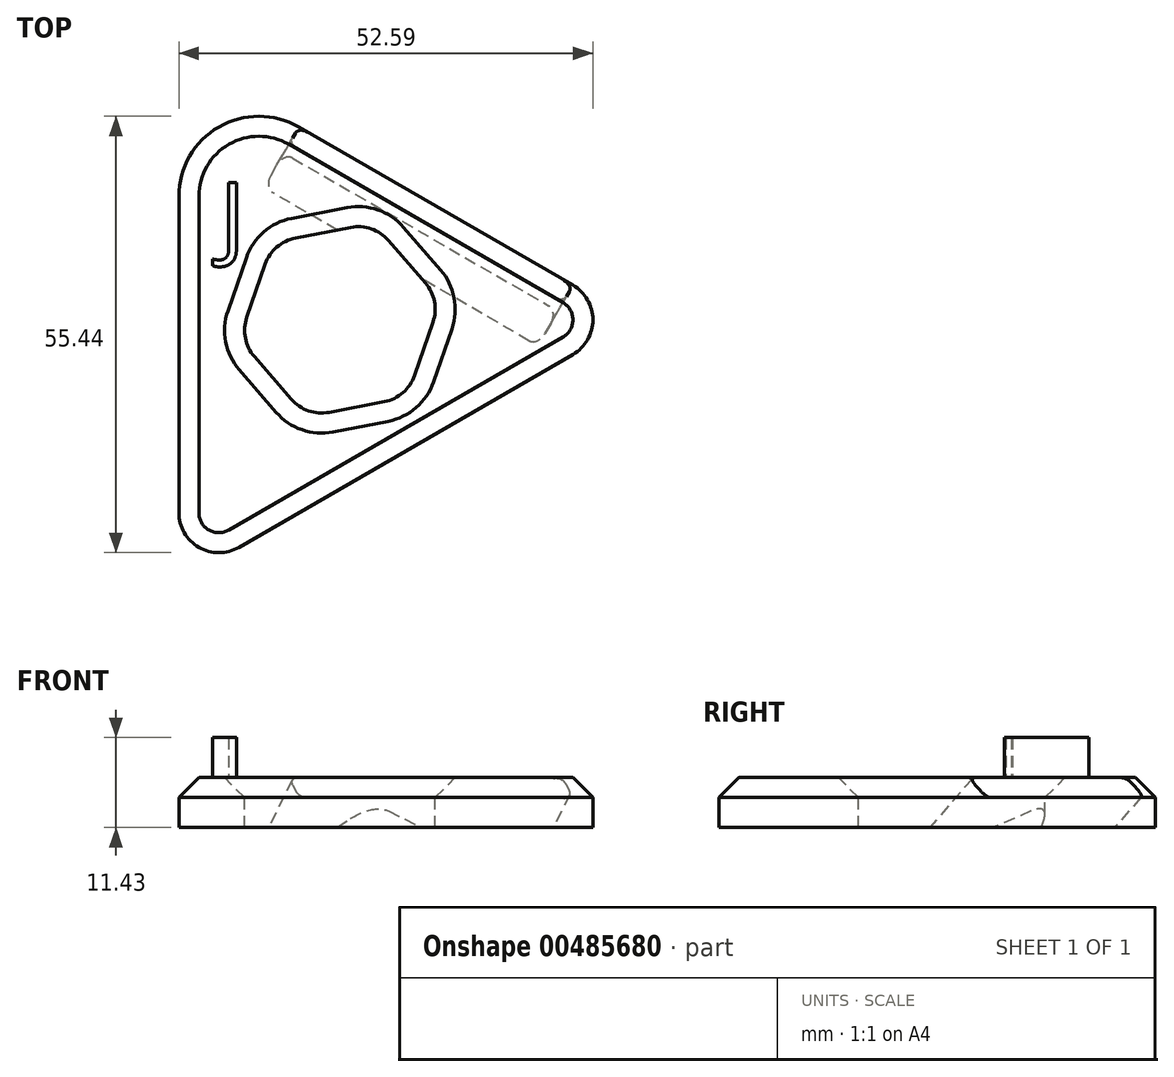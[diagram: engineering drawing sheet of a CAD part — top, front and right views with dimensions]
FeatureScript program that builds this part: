
annotation { "Feature Type Name" : "Feature", "Feature Type Description" : "" }
export const myFeature = defineFeature(function(context is Context, id is Id, definition is map)
    precondition{}
    {
        {
            var Q0;
            Q0=qCreatedBy(makeId("Top.planeOp"),FACE);
            var sketch = newSketch(context, id + "F0", { "sketchPlane" : qUnion([Q0])});
            skCircle(sketch, "E0.cCircle", {"center": v(0, 0) * mm, "radius": 38.45 * mm, "construction": true});
            skLineSegment(sketch, "E0.0", {"start": v(38.45, 0) * mm, "end": v(-19.22, -33.3) * mm});
            skLineSegment(sketch, "E0.1", {"start": v(-19.22, -33.3) * mm, "end": v(-19.22, 33.3) * mm});
            skLineSegment(sketch, "E0.2", {"start": v(-19.22, 33.3) * mm, "end": v(38.45, 0) * mm});
            skSolve(sketch);
        }
        {
            var Q0;
            Q0=makeQuery(id+"F0.imprint","IMPRINT",FACE,{"disambiguationData":[TD([[makeQuery(id+"F0.imprint","IMPRINT",EDGE,{"derivedFrom":sQuery(id+"F0.wireOp",EDGE,"E0.0")}),-1.0]])]});
            extrude(context, id + "F1", {"entities" : qUnion([Q0]), "depth" : 6.35 * mm});
        }
        {
            var Q0;
            Q0=makeQuery(id+"F1.opExtrude","SWEPT_EDGE",EDGE,{"disambiguationData":[OSD([sQuery(id+"F0.wireOp",EDGE,"E0.0"),sQuery(id+"F0.wireOp",EDGE,"E0.2")])]});
            fillet(context, id + "F2", {"entities" : qUnion([Q0]), "radius" : 5.08 * mm, "tangentPropagation" : true, "allowEdgeOverflow" : false});
        }
        {
            var Q0;
            Q0=makeQuery(id+"F1.opExtrude","SWEPT_EDGE",EDGE,{"disambiguationData":[OSD([sQuery(id+"F0.wireOp",EDGE,"E0.0"),sQuery(id+"F0.wireOp",EDGE,"E0.1")])]});
            fillet(context, id + "F3", {"entities" : qUnion([Q0]), "radius" : 5.08 * mm, "tangentPropagation" : true, "allowEdgeOverflow" : false});
        }
        {
            var Q0;
            Q0=makeQuery(id+"F1.opExtrude","SWEPT_EDGE",EDGE,{"disambiguationData":[OSD([sQuery(id+"F0.wireOp",EDGE,"E0.1"),sQuery(id+"F0.wireOp",EDGE,"E0.2")])]});
            fillet(context, id + "F4", {"entities" : qUnion([Q0]), "radius" : 10.16 * mm, "tangentPropagation" : true, "allowEdgeOverflow" : false});
        }
        {
            var Q0;
            Q0=makeQuery(id+"F1.opExtrude","CAP_EDGE",EDGE,{"disambiguationData":[OSD([sQuery(id+"F0.wireOp",EDGE,"E0.2")])],"isStart":false});
            chamfer(context, id + "F5", {"entities" : qUnion([Q0]), "width" : 2.54 * mm, "tangentPropagation" : true});
        }
        {
            var Q0;
            Q0=makeQuery(id+"F5.opChamfer","BLEND_FACE",FACE,{"disambiguationData":[OSD([sQuery(id+"F0.wireOp",EDGE,"E0.2")])]});
            var sketch = newSketch(context, id + "F6", { "sketchPlane" : qUnion([Q0])});
            skCircle(sketch, "E1", {"center": v(7.74, 6.62) * mm, "radius": 7.11 * mm, "construction": true});
            skSolve(sketch);
        }
        {
            var Q0;
            {var subQ0=sQuery(id+"F6.wireOp",EDGE,"E1");var subQ1=sQuery(id+"F0.wireOp",EDGE,"E0.2");var subQ2=makeQuery(id+"F1.opExtrude","CAP_EDGE",EDGE,{"disambiguationData":[OSD([subQ1])],"isStart":false});var subQ3=makeQuery(id+"F5.opChamfer","BLEND_EDGE",EDGE,{"blendedFrom":[subQ2,makeQuery(id+"F1.opExtrude","SWEPT_FACE",FACE,{"disambiguationData":[OSD([subQ1])]})],"blendedInto":[makeQuery(id+"F1.opExtrude","SWEPT_FACE",FACE,{"disambiguationData":[OSD([subQ1])]})]});var subQ4=makeQuery(id+"F6.imprint","INTERSECT",VERTEX,{"disambiguationData":[OD(0.0)],"derivedFrom":[subQ3,subQ0]});Q0=makeQuery(id+"F6.imprint","IMPRINT",FACE,{"disambiguationData":[TD([[makeQuery(id+"F6.imprint","IMPRINT",EDGE,{"disambiguationData":[TD([[subQ4,-1.0]])],"derivedFrom":subQ3}),-1.0]])]});}
            var Q1;
            {var subQ0=sQuery(id+"F6.wireOp",EDGE,"E1");var subQ1=sQuery(id+"F0.wireOp",EDGE,"E0.2");var subQ2=makeQuery(id+"F5.opChamfer","BLEND_EDGE",EDGE,{"blendedFrom":[makeQuery(id+"F1.opExtrude","CAP_EDGE",EDGE,{"disambiguationData":[OSD([subQ1])],"isStart":false}),makeQuery(id+"F1.opExtrude","CAP_FACE",FACE,{"disambiguationData":[OSD([sQuery(id+"F0.wireOp",EDGE,"E0.0"),sQuery(id+"F0.wireOp",EDGE,"E0.1"),subQ1])],"isStart":false})],"blendedInto":[makeQuery(id+"F1.opExtrude","CAP_FACE",FACE,{"disambiguationData":[OSD([sQuery(id+"F0.wireOp",EDGE,"E0.0"),sQuery(id+"F0.wireOp",EDGE,"E0.1"),subQ1])],"isStart":false})]});var subQ3=makeQuery(id+"F6.imprint","INTERSECT",VERTEX,{"disambiguationData":[OD(0.0)],"derivedFrom":[subQ2,subQ0]});Q1=makeQuery(id+"F6.imprint","IMPRINT",FACE,{"disambiguationData":[TD([[makeQuery(id+"F6.imprint","IMPRINT",EDGE,{"disambiguationData":[TD([[subQ3,-1.0]])],"derivedFrom":subQ0}),1.0]])]});}
            var Q2;
            {var subQ0=sQuery(id+"F6.wireOp",EDGE,"E1");var subQ1=sQuery(id+"F0.wireOp",EDGE,"E0.2");var subQ2=makeQuery(id+"F5.opChamfer","BLEND_EDGE",EDGE,{"blendedFrom":[makeQuery(id+"F1.opExtrude","CAP_EDGE",EDGE,{"disambiguationData":[OSD([subQ1])],"isStart":false}),makeQuery(id+"F1.opExtrude","SWEPT_FACE",FACE,{"disambiguationData":[OSD([subQ1])]})],"blendedInto":[makeQuery(id+"F1.opExtrude","SWEPT_FACE",FACE,{"disambiguationData":[OSD([subQ1])]})]});var subQ3=makeQuery(id+"F6.imprint","INTERSECT",VERTEX,{"disambiguationData":[OD(0.0)],"derivedFrom":[subQ2,subQ0]});Q2=makeQuery(id+"F6.imprint","IMPRINT",FACE,{"disambiguationData":[TD([[makeQuery(id+"F6.imprint","IMPRINT",EDGE,{"disambiguationData":[TD([[subQ3,1.0]])],"derivedFrom":subQ0}),1.0]])]});}
            extrude(context, id + "F7", {"entities" : qUnion([Q0, Q1, Q2]), "operationType" : NewBodyOperationType.REMOVE, "endBound" : BoundingType.THROUGH_ALL, "oppositeDirection" : true, "depth" : 25.4 * mm, "hasSecondDirection" : true, "secondDirectionOppositeDirection" : false, "secondDirectionDepth" : 50.8 * mm});
        }
        {
            var Q0;
            Q0=makeQuery(id+"F1.opExtrude","CAP_FACE",FACE,{"disambiguationData":[OSD([sQuery(id+"F0.wireOp",EDGE,"E0.0"),sQuery(id+"F0.wireOp",EDGE,"E0.1"),sQuery(id+"F0.wireOp",EDGE,"E0.2")])],"isStart":false});
            var sketch = newSketch(context, id + "F8", { "sketchPlane" : qUnion([Q0])});
            skCircle(sketch, "E2.cCircle", {"center": v(1.23, 0) * mm, "radius": 13.02 * mm, "construction": true});
            skLineSegment(sketch, "E2.0", {"start": v(9.76, -9.84) * mm, "end": v(-3.03, -12.3) * mm});
            skLineSegment(sketch, "E2.1", {"start": v(-3.03, -12.3) * mm, "end": v(-11.55, -2.46) * mm});
            skLineSegment(sketch, "E2.2", {"start": v(-11.55, -2.46) * mm, "end": v(-7.3, 9.84) * mm});
            skLineSegment(sketch, "E2.3", {"start": v(-7.3, 9.84) * mm, "end": v(5.49, 12.3) * mm});
            skLineSegment(sketch, "E2.4", {"start": v(5.49, 12.3) * mm, "end": v(14.01, 2.46) * mm});
            skLineSegment(sketch, "E2.5", {"start": v(14.01, 2.46) * mm, "end": v(9.76, -9.84) * mm});
            skSolve(sketch);
        }
        {
            var Q0;
            Q0=makeQuery(id+"F8.imprint","IMPRINT",FACE,{"disambiguationData":[TD([[makeQuery(id+"F8.imprint","IMPRINT",EDGE,{"derivedFrom":sQuery(id+"F8.wireOp",EDGE,"E2.0")}),-1.0]])]});
            extrude(context, id + "F9", {"entities" : qUnion([Q0]), "operationType" : NewBodyOperationType.REMOVE, "endBound" : BoundingType.THROUGH_ALL, "depth" : 25.4 * mm, "hasSecondDirection" : true, "secondDirectionOppositeDirection" : true, "secondDirectionDepth" : 25.4 * mm});
        }
        {
            var Q0;
            Q0=makeQuery(id+"F9.boolean.opBoolean","COPY",EDGE,{"derivedFrom":makeQuery(id+"F9.opExtrude","SWEPT_EDGE",EDGE,{"disambiguationData":[OSD([sQuery(id+"F8.wireOp",EDGE,"E2.1"),sQuery(id+"F8.wireOp",EDGE,"E2.2")])]})});
            var Q1;
            Q1=makeQuery(id+"F9.boolean.opBoolean","COPY",EDGE,{"derivedFrom":makeQuery(id+"F9.opExtrude","SWEPT_EDGE",EDGE,{"disambiguationData":[OSD([sQuery(id+"F8.wireOp",EDGE,"E2.2"),sQuery(id+"F8.wireOp",EDGE,"E2.3")])]})});
            var Q2;
            Q2=makeQuery(id+"F9.boolean.opBoolean","COPY",EDGE,{"derivedFrom":makeQuery(id+"F9.opExtrude","SWEPT_EDGE",EDGE,{"disambiguationData":[OSD([sQuery(id+"F8.wireOp",EDGE,"E2.0"),sQuery(id+"F8.wireOp",EDGE,"E2.1")])]})});
            var Q3;
            Q3=makeQuery(id+"F9.boolean.opBoolean","COPY",EDGE,{"derivedFrom":makeQuery(id+"F9.opExtrude","SWEPT_EDGE",EDGE,{"disambiguationData":[OSD([sQuery(id+"F8.wireOp",EDGE,"E2.0"),sQuery(id+"F8.wireOp",EDGE,"E2.5")])]})});
            var Q4;
            Q4=makeQuery(id+"F9.boolean.opBoolean","COPY",EDGE,{"derivedFrom":makeQuery(id+"F9.opExtrude","SWEPT_EDGE",EDGE,{"disambiguationData":[OSD([sQuery(id+"F8.wireOp",EDGE,"E2.3"),sQuery(id+"F8.wireOp",EDGE,"E2.4")])]})});
            var Q5;
            Q5=makeQuery(id+"F9.boolean.opBoolean","COPY",EDGE,{"derivedFrom":makeQuery(id+"F9.opExtrude","SWEPT_EDGE",EDGE,{"disambiguationData":[OSD([sQuery(id+"F8.wireOp",EDGE,"E2.4"),sQuery(id+"F8.wireOp",EDGE,"E2.5")])]})});
            fillet(context, id + "F10", {"entities" : qUnion([Q0, Q1, Q2, Q3, Q4, Q5]), "radius" : 5.08 * mm, "tangentPropagation" : true, "allowEdgeOverflow" : false});
        }
        {
            var Q0;
            Q0=makeQuery(id+"F10.opFillet","BLEND_EDGE",EDGE,{"blendedFrom":[makeQuery(id+"F9.boolean.opBoolean","COPY",EDGE,{"derivedFrom":makeQuery(id+"F9.opExtrude","SWEPT_EDGE",EDGE,{"disambiguationData":[OSD([sQuery(id+"F8.wireOp",EDGE,"E2.0"),sQuery(id+"F8.wireOp",EDGE,"E2.1")])]})}),makeQuery(id+"F1.opExtrude","CAP_FACE",FACE,{"disambiguationData":[OSD([sQuery(id+"F0.wireOp",EDGE,"E0.0"),sQuery(id+"F0.wireOp",EDGE,"E0.1"),sQuery(id+"F0.wireOp",EDGE,"E0.2")])],"isStart":false})],"blendedInto":[makeQuery(id+"F1.opExtrude","CAP_FACE",FACE,{"disambiguationData":[OSD([sQuery(id+"F0.wireOp",EDGE,"E0.0"),sQuery(id+"F0.wireOp",EDGE,"E0.1"),sQuery(id+"F0.wireOp",EDGE,"E0.2")])],"isStart":false})]});
            chamfer(context, id + "F11", {"entities" : qUnion([Q0]), "width" : 2.54 * mm, "tangentPropagation" : true});
        }
        {
            var Q0;
            {var subQ0=sQuery(id+"F0.wireOp",EDGE,"E0.2");var subQ1=sQuery(id+"F0.wireOp",EDGE,"E0.1");var subQ2=sQuery(id+"F0.wireOp",EDGE,"E0.0");var subQ3=makeQuery(id+"F1.opExtrude","CAP_FACE",FACE,{"disambiguationData":[OSD([subQ2,subQ1,subQ0])],"isStart":false});var subQ4=makeQuery(id+"F1.opExtrude","CAP_EDGE",EDGE,{"disambiguationData":[OSD([subQ0])],"isStart":false});Q0=makeQuery(id+"F7.boolean.opBoolean","COPY",EDGE,{"derivedFrom":makeQuery(id+"F7.opExtrude","SWEPT_EDGE",EDGE,{"disambiguationData":[OSD([subQ2,subQ1,subQ0]),TDD([makeQuery(id+"F6.imprint","INTERSECT",VERTEX,{"derivedFrom":[makeQuery(id+"F5.opChamfer","BLEND_EDGE",EDGE,{"blendedFrom":[makeQuery(id+"F4.opFillet","BLEND_EDGE",EDGE,{"blendedFrom":[makeQuery(id+"F1.opExtrude","SWEPT_EDGE",EDGE,{"disambiguationData":[OSD([subQ1,subQ0])]}),subQ3],"blendedInto":[subQ3]}),subQ4],"blendedInto":[]}),makeQuery(id+"F5.opChamfer","BLEND_EDGE",EDGE,{"blendedFrom":[subQ4,subQ3],"blendedInto":[subQ3]})]})])]})});}
            var Q1;
            {var subQ0=sQuery(id+"F0.wireOp",EDGE,"E0.2");var subQ1=sQuery(id+"F0.wireOp",EDGE,"E0.1");var subQ2=sQuery(id+"F0.wireOp",EDGE,"E0.0");var subQ3=makeQuery(id+"F1.opExtrude","CAP_FACE",FACE,{"disambiguationData":[OSD([subQ2,subQ1,subQ0])],"isStart":false});var subQ4=makeQuery(id+"F1.opExtrude","CAP_EDGE",EDGE,{"disambiguationData":[OSD([subQ0])],"isStart":false});Q1=makeQuery(id+"F7.boolean.opBoolean","COPY",EDGE,{"derivedFrom":makeQuery(id+"F7.opExtrude","SWEPT_EDGE",EDGE,{"disambiguationData":[OSD([subQ2,subQ1,subQ0]),TDD([makeQuery(id+"F6.imprint","INTERSECT",VERTEX,{"derivedFrom":[makeQuery(id+"F5.opChamfer","BLEND_EDGE",EDGE,{"blendedFrom":[makeQuery(id+"F2.opFillet","BLEND_EDGE",EDGE,{"blendedFrom":[makeQuery(id+"F1.opExtrude","SWEPT_EDGE",EDGE,{"disambiguationData":[OSD([subQ2,subQ0])]}),subQ3],"blendedInto":[subQ3]}),subQ4],"blendedInto":[]}),makeQuery(id+"F5.opChamfer","BLEND_EDGE",EDGE,{"blendedFrom":[subQ4,subQ3],"blendedInto":[subQ3]})]})])]})});}
            var Q2;
            {var subQ0=sQuery(id+"F0.wireOp",EDGE,"E0.2");var subQ1=makeQuery(id+"F1.opExtrude","CAP_EDGE",EDGE,{"disambiguationData":[OSD([subQ0])],"isStart":false});var subQ2=sQuery(id+"F0.wireOp",EDGE,"E0.1");var subQ3=sQuery(id+"F0.wireOp",EDGE,"E0.0");Q2=makeQuery(id+"F7.boolean.opBoolean","COPY",EDGE,{"derivedFrom":makeQuery(id+"F7.opExtrude","SWEPT_EDGE",EDGE,{"disambiguationData":[OSD([subQ3,subQ2,subQ0]),TDD([makeQuery(id+"F6.imprint","INTERSECT",VERTEX,{"derivedFrom":[makeQuery(id+"F5.opChamfer","BLEND_EDGE",EDGE,{"blendedFrom":[makeQuery(id+"F2.opFillet","BLEND_EDGE",EDGE,{"blendedFrom":[makeQuery(id+"F1.opExtrude","SWEPT_EDGE",EDGE,{"disambiguationData":[OSD([subQ3,subQ0])]}),makeQuery(id+"F1.opExtrude","CAP_FACE",FACE,{"disambiguationData":[OSD([subQ3,subQ2,subQ0])],"isStart":false})],"blendedInto":[makeQuery(id+"F1.opExtrude","CAP_FACE",FACE,{"disambiguationData":[OSD([subQ3,subQ2,subQ0])],"isStart":false})]}),subQ1],"blendedInto":[]}),makeQuery(id+"F5.opChamfer","BLEND_EDGE",EDGE,{"blendedFrom":[subQ1,makeQuery(id+"F1.opExtrude","SWEPT_FACE",FACE,{"disambiguationData":[OSD([subQ0])]})],"blendedInto":[makeQuery(id+"F1.opExtrude","SWEPT_FACE",FACE,{"disambiguationData":[OSD([subQ0])]})]})]})])]})});}
            var Q3;
            {var subQ0=sQuery(id+"F0.wireOp",EDGE,"E0.2");var subQ1=makeQuery(id+"F1.opExtrude","CAP_EDGE",EDGE,{"disambiguationData":[OSD([subQ0])],"isStart":false});var subQ2=sQuery(id+"F0.wireOp",EDGE,"E0.1");var subQ3=sQuery(id+"F0.wireOp",EDGE,"E0.0");Q3=makeQuery(id+"F7.boolean.opBoolean","COPY",EDGE,{"derivedFrom":makeQuery(id+"F7.opExtrude","SWEPT_EDGE",EDGE,{"disambiguationData":[OSD([subQ3,subQ2,subQ0]),TDD([makeQuery(id+"F6.imprint","INTERSECT",VERTEX,{"derivedFrom":[makeQuery(id+"F5.opChamfer","BLEND_EDGE",EDGE,{"blendedFrom":[makeQuery(id+"F4.opFillet","BLEND_EDGE",EDGE,{"blendedFrom":[makeQuery(id+"F1.opExtrude","SWEPT_EDGE",EDGE,{"disambiguationData":[OSD([subQ2,subQ0])]}),makeQuery(id+"F1.opExtrude","CAP_FACE",FACE,{"disambiguationData":[OSD([subQ3,subQ2,subQ0])],"isStart":false})],"blendedInto":[makeQuery(id+"F1.opExtrude","CAP_FACE",FACE,{"disambiguationData":[OSD([subQ3,subQ2,subQ0])],"isStart":false})]}),subQ1],"blendedInto":[]}),makeQuery(id+"F5.opChamfer","BLEND_EDGE",EDGE,{"blendedFrom":[subQ1,makeQuery(id+"F1.opExtrude","SWEPT_FACE",FACE,{"disambiguationData":[OSD([subQ0])]})],"blendedInto":[makeQuery(id+"F1.opExtrude","SWEPT_FACE",FACE,{"disambiguationData":[OSD([subQ0])]})]})]})])]})});}
            fillet(context, id + "F12", {"entities" : qUnion([Q0, Q1, Q2, Q3]), "radius" : 1.27 * mm, "tangentPropagation" : true, "allowEdgeOverflow" : false});
        }
        {
            var Q0;
            Q0=makeQuery(id+"F1.opExtrude","CAP_FACE",FACE,{"disambiguationData":[OSD([sQuery(id+"F0.wireOp",EDGE,"E0.0"),sQuery(id+"F0.wireOp",EDGE,"E0.1"),sQuery(id+"F0.wireOp",EDGE,"E0.2")])],"isStart":false});
            var sketch = newSketch(context, id + "F13", { "sketchPlane" : qUnion([Q0])});
            skText(sketch, "E3", { "text": "J", "fontName": "OpenSans-Regular.ttf"});
            const initialGuessF13  = {"E3": [-0.01399, 0.00896, 1, 0, 0.00856]};
            skSetInitialGuess(sketch, initialGuessF13);
            skSolve(sketch);
        }
        {
            var Q0;
            Q0 = qSketchRegion(id + "F13", true);
            extrude(context, id + "F14", {"entities" : qUnion([Q0]), "operationType" : NewBodyOperationType.ADD, "depth" : 5.08 * mm});
        }
    });
